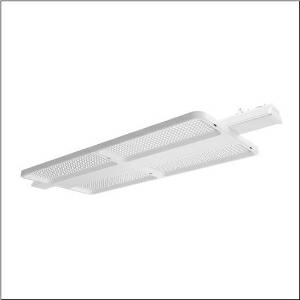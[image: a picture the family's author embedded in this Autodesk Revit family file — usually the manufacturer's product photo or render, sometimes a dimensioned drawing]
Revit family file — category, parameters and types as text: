
# Revit family: highbay_21_fur_licross_r__tragschiene_maxi_52hn11db4qla02_300a
name_source: partatom
category: Lighting Fixtures
units: mm (PartAtom-declared; Revit-internal decimal feet)

## family parameters
Cut with Voids When Loaded = No
Host = Face
Light Source = No
Part Type = Normal
Room Calculation Point = No
Round Connector Dimension = Use Diameter
Shared = No

## types (1)
- --- (1 x LED, 38000 lm, 198.2 W, 4000K)
    Apparent Load = 198 VA
    CIE Flux Codes = 89 97 99 100 100
    Color Rendering = 80
    Color Temperature = 4000K
    Default Elevation = 1800 mm
    Description = high bay luminaire Highbay 21 for Licross® trunking rail maxi; direct symmetric narrow distribution, light control with lens of PMMA; UGR ≤ 19 (X = 4H | Y = 8H | S = 0.25H | reflection values 70/50/20); luminous flux: 38.000lm; light colour: 840, colour temperature: 4000K, MacAdam ≤ 3 SDCM (initial), colour rendering: CRI > 80; luminous efficacy: 191,7lm/W; rated service life: 75.000h (L80/B50) at AT= ta max; control: Bluetooth® Mesh; for wireless networking: Node luminaire for setting up a local control solution without a higher-level application controller, intelligence completely in the luminaire; no control line such as DALI between the Node multi-sensor luminaires and Nodes is required, wireless integration of other Node luminaires and Node multi-sensor luminaires into the network is possible; number of Node luminaires in the project can be expanded as required, network sizes > 300 Nodes can be realized; can also be connected to lighting or building automation via various gateways upon request; integrated DALI2 ECG provides luminaire data (according to IEC62386, Part 251), energy data (Part 252), and monitoring and analytics data (Part 253) to higher-level systems for further processing; luminaire connection: plug, 5-pole, with phase selectionmains connection: 230..240V, AC 50/60Hz; connected load: 198,2W; protection rating (complete): IP64; insulation class (complete): insulation class I (protective earthing); protection symbol: D; impact resistance: IK08; certification: CE, ENEC, VDE, UKCA; internal wiring halogen-free; luminaire LABS conformity tested according to VDMA 24364:2018-05; corresponds to IFS (International Featured Standards) requirements for safety and quality in the food industry; housing frame of high-performance plastic PA6, matt traffic white (RAL 9016); cover of PMMA; fixing on rail side of steel, galvanised, white; blank cover of PC/ABS, traffic white (RAL 9016); dimension (LxWxH): 1.250 x 442 x 71mm; permissible operating ambient temperature: -20..+40°C (reducing of maximum allowable ambient temperature of 5°C with ceiling mounting); packaging unit: 1 piece
    Height = 72 mm  [stored 0.23622 ft]
    Lamp = 1 x LED
    Lamp Light Flux = 38000 lm
    Lamp Power = 198.2 W
    Lamp count = 1
    Length = 946 mm
    Luminous efficacy = 192 lm/W
    Manufacturer = Siteco
    ModVariant = No
    Model = 52HN11DB4QLA02
    Mounting Place = Ceiling
    Mounting Type = Pendant
    Number of Poles = 1
    OnlyDefault = Yes
    Power Factor = 1
    Product Name = Highbay 21 für Licross® Tragschiene maxi
    Product group = high bay luminaire
    ProductGroupID = 901
    Protection Class = Protection class I
    Protection Degree = IP 64
    RLX_Detail_Level = 1
    RLX_Emergency_Light_Flux = 0 lm
    RLX_Emergency_Type = 0
    RLX_Emergency_Type_DB = No
    RlxData = <blob elided: 131269 chars, md5=d6202740>
    Socket = socket
    Standby Power = 0 W
    System Light Flux = 38001 lm
    System Power = 198 W
    Type Comments = factory setting: luminous flux: 100 % | dim-lin: 254 | 918 mA
    Type Image = l_1361711.jpg
    URL = http://relux.com
    VarID = @adj_009519
    Voltage = 0 V
    Weight = 0.00 kg
    Width = 442 mm

note: [stored X ft] marks values corroborated as IEEE doubles in the binary element streams (Revit-internal decimal feet)

## geometry (parser evidence)
native form markers: Blend x4, Sweep x11
no freeform markers — native parametric forms only
